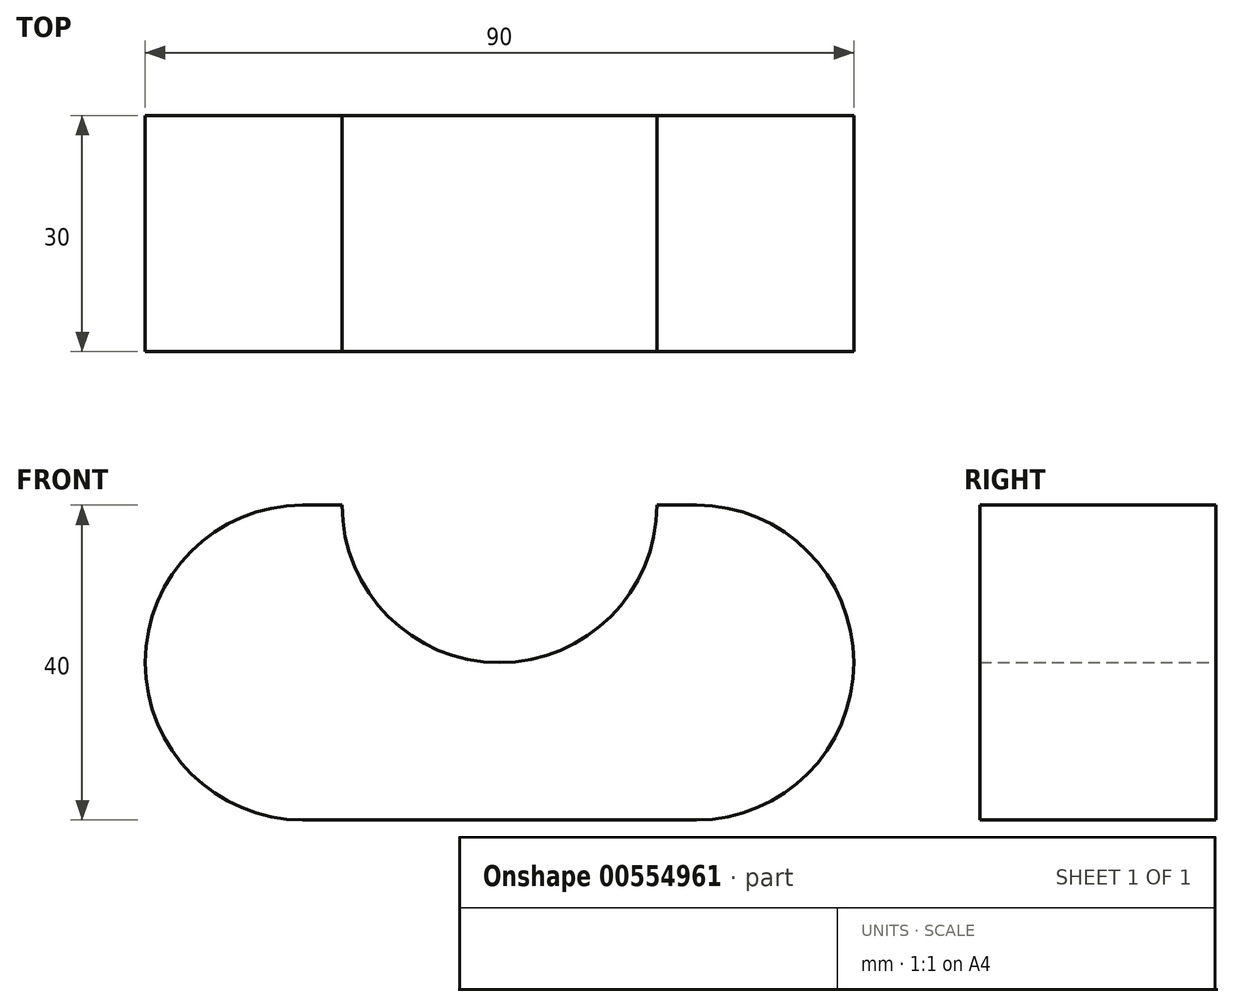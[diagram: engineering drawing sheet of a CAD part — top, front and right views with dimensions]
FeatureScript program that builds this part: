
annotation { "Feature Type Name" : "Feature", "Feature Type Description" : "" }
export const myFeature = defineFeature(function(context is Context, id is Id, definition is map)
    precondition{}
    {
        {
            var Q0;
            Q0=qCreatedBy(makeId("Front.planeOp"),FACE);
            var sketch = newSketch(context, id + "F0", { "sketchPlane" : qUnion([Q0])});
            skArc(sketch, "E0", {"start": v(-37.92, 10.07) * mm, "mid": v(-17.92, -9.93) * mm, "end": v(2.08, 10.07) * mm});
            skLineSegment(sketch, "E1", {"start": v(2.08, 10.07) * mm, "end": v(7.08, 10.07) * mm});
            skLineSegment(sketch, "E2", {"start": v(-37.92, 10.07) * mm, "end": v(-42.92, 10.07) * mm});
            skLineSegment(sketch, "E3", {"start": v(-42.92, -29.93) * mm, "end": v(7.08, -29.93) * mm});
            skArc(sketch, "E4", {"start": v(7.08, -29.93) * mm, "mid": v(27.08, -9.93) * mm, "end": v(7.08, 10.07) * mm});
            skArc(sketch, "E5", {"start": v(-42.92, 10.07) * mm, "mid": v(-62.92, -9.93) * mm, "end": v(-42.92, -29.93) * mm});
            skSolve(sketch);
        }
        {
            var Q0;
            Q0 = qSketchRegion(id + "F0", true);
            extrude(context, id + "F1", {"entities" : qUnion([Q0]), "depth" : 30 * mm, "offsetDistance" : 25 * mm});
        }
    });
